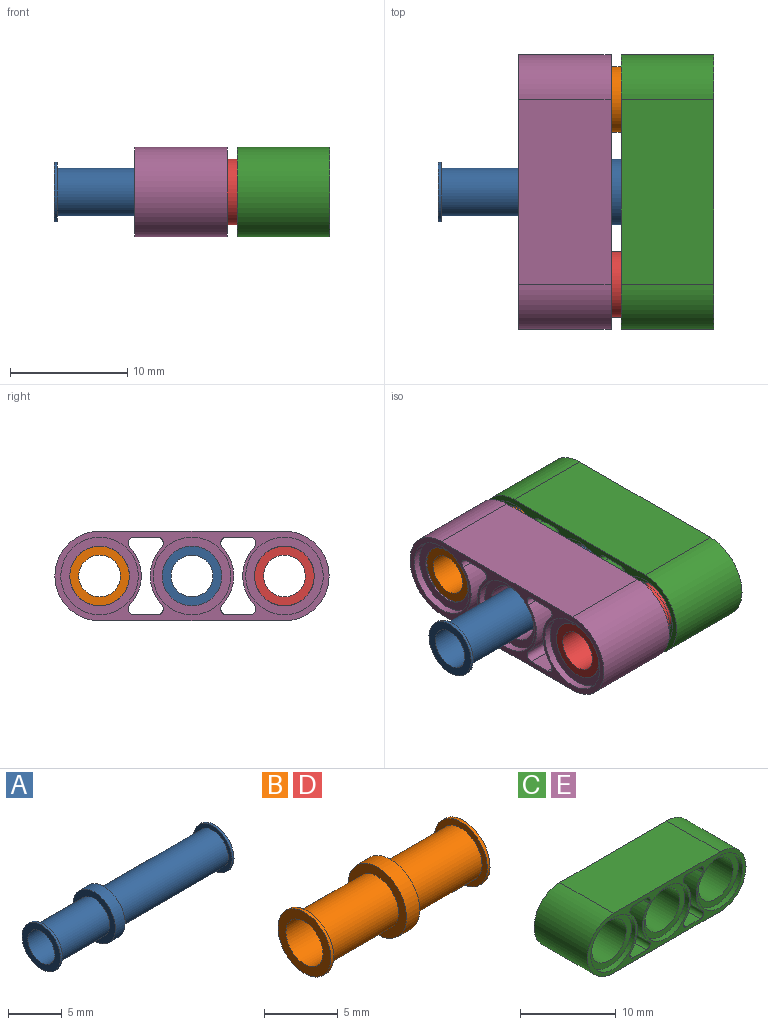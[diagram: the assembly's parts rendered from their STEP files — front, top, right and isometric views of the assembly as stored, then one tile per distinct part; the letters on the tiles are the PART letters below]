
ASSEMBLY  parts=5 mates=4
PART A: 12 faces, bbox 22.9x5.6x5.6 mm
  f0: cylinder r=2.54mm len=5.08mm, axis (-1,0,0), area 4.1mm2, adj f1,f11
  f1: plane 5.08x5.08mm, normal (1,0,0), area 7.3mm2, adj f0,f2
  f2: cylinder r=2.03mm len=6.73mm, axis (-1,0,0), area 85.9mm2, adj f1,f3
  f3: plane 5.59x5.59mm, normal (-1,0,0), area 11.6mm2, adj f2,f4
  f4: cylinder r=2.79mm len=5.59mm, axis (-1,0,0), area 22.3mm2, adj f3,f5
  f5: plane 5.59x5.59mm, normal (1,0,0), area 11.6mm2, adj f4,f6
  f6: cylinder r=2.03mm len=14.35mm, axis (-1,0,0), area 183.2mm2, adj f5,f7
  f7: plane 5.08x5.08mm, normal (-1,0,0), area 7.3mm2, adj f6,f8
  f8: cylinder r=2.54mm len=5.08mm, axis (-1,0,0), area 4.1mm2, adj f7,f9
  f9: plane 5.08x5.08mm, normal (1,0,0), area 10.3mm2, adj f8,f10
  f10: cylinder r=1.78mm len=22.86mm, axis (-1,0,0), area 255.4mm2, adj f9,f11
  f11: plane 5.08x5.08mm, normal (-1,0,0), area 10.3mm2, adj f0,f10
PART B: 12 faces, bbox 15.2x5.6x5.6 mm
  f0: cylinder r=2.54mm len=5.08mm, axis (-1,0,0), area 4.1mm2, adj f1,f11
  f1: plane 5.08x5.08mm, normal (1,0,0), area 7.3mm2, adj f0,f2
  f2: cylinder r=2.03mm len=6.73mm, axis (-1,0,0), area 85.9mm2, adj f1,f3
  f3: plane 5.59x5.59mm, normal (-1,0,0), area 11.6mm2, adj f2,f4
  f4: cylinder r=2.79mm len=5.59mm, axis (-1,0,0), area 22.3mm2, adj f3,f5
  f5: plane 5.59x5.59mm, normal (1,0,0), area 11.6mm2, adj f4,f6
  f6: cylinder r=2.03mm len=6.73mm, axis (-1,0,0), area 85.9mm2, adj f5,f7
  f7: plane 5.08x5.08mm, normal (-1,0,0), area 7.3mm2, adj f6,f8
  f8: cylinder r=2.54mm len=5.08mm, axis (-1,0,0), area 4.1mm2, adj f7,f9
  f9: plane 5.08x5.08mm, normal (1,0,0), area 10.3mm2, adj f8,f10
  f10: cylinder r=1.78mm len=15.24mm, axis (-1,0,0), area 170.3mm2, adj f9,f11
  f11: plane 5.08x5.08mm, normal (-1,0,0), area 10.3mm2, adj f0,f10
PART C: 37 faces, bbox 23.4x7.9x7.6 mm
  f0: cylinder r=2.54mm len=6.6mm, axis (0,-1,0), area 105.4mm2, adj f11,f32
  f1: plane 7.87x1.97mm, normal (0,0,1), area 15.5mm2, adj f2,f9,f24,f30
  f2: cylinder r=0.51mm len=7.87mm, axis (0,-1,0), area 9.3mm2, adj f1,f3,f9,f30
  f3: cylinder r=3.56mm len=7.87mm, axis (0,-1,0), area 42.5mm2, adj f2,f4,f9,f30
  f4: cylinder r=0.51mm len=7.87mm, axis (0,-1,0), area 9.3mm2, adj f3,f5,f9,f30
  f5: plane 7.87x1.97mm, normal (0,0,-1), area 15.5mm2, adj f4,f9,f22,f30
  f6: plane 15.75x7.87mm, normal (0,0,1), area 124mm2, adj f7,f9,f18,f30
  f7: cylinder r=3.81mm len=7.87mm, axis (0,-1,0), area 94.2mm2, adj f6,f8,f9,f30
  f8: plane 15.75x7.87mm, normal (0,0,-1), area 124mm2, adj f7,f9,f18,f30
  f9: plane 23.37x7.62mm, normal (0,-1,0), area 39.8mm2, adj f1,f2,f3,f4,f5,f6,f7,f8
  f10: cylinder r=3.3mm len=6.6mm, axis (0,-1,0), area 13.2mm2, adj f9,f11
  f11: plane 6.6x6.6mm, normal (0,-1,0), area 14mm2, adj f0,f10
  f12: cylinder r=2.54mm len=6.6mm, axis (0,-1,0), area 105.4mm2, adj f20,f34
  f13: plane 7.87x1.97mm, normal (0,0,1), area 15.5mm2, adj f9,f14,f25,f30
  f14: cylinder r=0.51mm len=7.87mm, axis (0,-1,0), area 9.3mm2, adj f9,f13,f15,f30
  f15: cylinder r=3.56mm len=7.87mm, axis (0,-1,0), area 42.5mm2, adj f9,f14,f16,f30
  f16: cylinder r=0.51mm len=7.87mm, axis (0,-1,0), area 9.3mm2, adj f9,f15,f17,f30
  f17: plane 7.87x1.97mm, normal (0,0,-1), area 15.5mm2, adj f9,f16,f27,f30
  f18: cylinder r=3.81mm len=7.87mm, axis (0,-1,0), area 94.2mm2, adj f6,f8,f9,f30
  f19: cylinder r=3.3mm len=6.6mm, axis (0,-1,0), area 13.2mm2, adj f9,f20
  f20: plane 6.6x6.6mm, normal (0,-1,0), area 14mm2, adj f12,f19
  f21: cylinder r=2.54mm len=6.6mm, axis (0,-1,0), area 105.4mm2, adj f29,f36
  f22: cylinder r=0.51mm len=7.87mm, axis (0,-1,0), area 9.3mm2, adj f5,f9,f23,f30
  f23: cylinder r=3.56mm len=7.87mm, axis (0,-1,0), area 42.5mm2, adj f9,f22,f24,f30
  f24: cylinder r=0.51mm len=7.87mm, axis (0,-1,0), area 9.3mm2, adj f1,f9,f23,f30
  f25: cylinder r=0.51mm len=7.87mm, axis (0,-1,0), area 9.3mm2, adj f9,f13,f26,f30
  f26: cylinder r=3.56mm len=7.87mm, axis (0,-1,0), area 42.5mm2, adj f9,f25,f27,f30
  f27: cylinder r=0.51mm len=7.87mm, axis (0,-1,0), area 9.3mm2, adj f9,f17,f26,f30
  f28: cylinder r=3.3mm len=6.6mm, axis (0,-1,0), area 13.2mm2, adj f9,f29
  f29: plane 6.6x6.6mm, normal (0,-1,0), area 14mm2, adj f21,f28
  f30: plane 23.37x7.62mm, normal (0,1,0), area 39.8mm2, adj f1,f2,f3,f4,f5,f6,f7,f8
  f31: cylinder r=3.3mm len=6.6mm, axis (0,1,0), area 13.2mm2, adj f30,f32
  f32: plane 6.6x6.6mm, normal (0,1,0), area 14mm2, adj f0,f31
  f33: cylinder r=3.3mm len=6.6mm, axis (0,1,0), area 13.2mm2, adj f30,f34
  f34: plane 6.6x6.6mm, normal (0,1,0), area 14mm2, adj f12,f33
  f35: cylinder r=3.3mm len=6.6mm, axis (0,1,0), area 13.2mm2, adj f30,f36
  f36: plane 6.6x6.6mm, normal (0,1,0), area 14mm2, adj f21,f35
PART D: same geometry as B
PART E: same geometry as C
PLACE A rot(axis=(0,1,0),180deg) t=(16.98,-2.99,16.98)mm
PLACE B rot(axis=(0,0.71,-0.71),180deg) t=(16.98,4.89,16.98)mm
PLACE C rot(axis=(0,0,-1),90deg) t=(9.74,-2.99,16.98)mm
PLACE D t=(1.62,-10.86,16.98)mm
PLACE E rot(axis=(0,0,-1),90deg) t=(0.98,-2.99,16.98)mm
MATE fastened D.f0 <-> D.f0  axis (1,0,0) through (16.86,-10.86,16.98)mm
MATE fastened B.f0 <-> C.f12  axis (1,0,0) through (16.98,4.89,16.98)mm
MATE fastened E.f0 <-> D.f0  axis (-1,0,0) through (1.62,-10.86,16.98)mm
MATE fastened A.f0 <-> C.f21  axis (1,0,0) through (16.98,-2.99,16.98)mm
